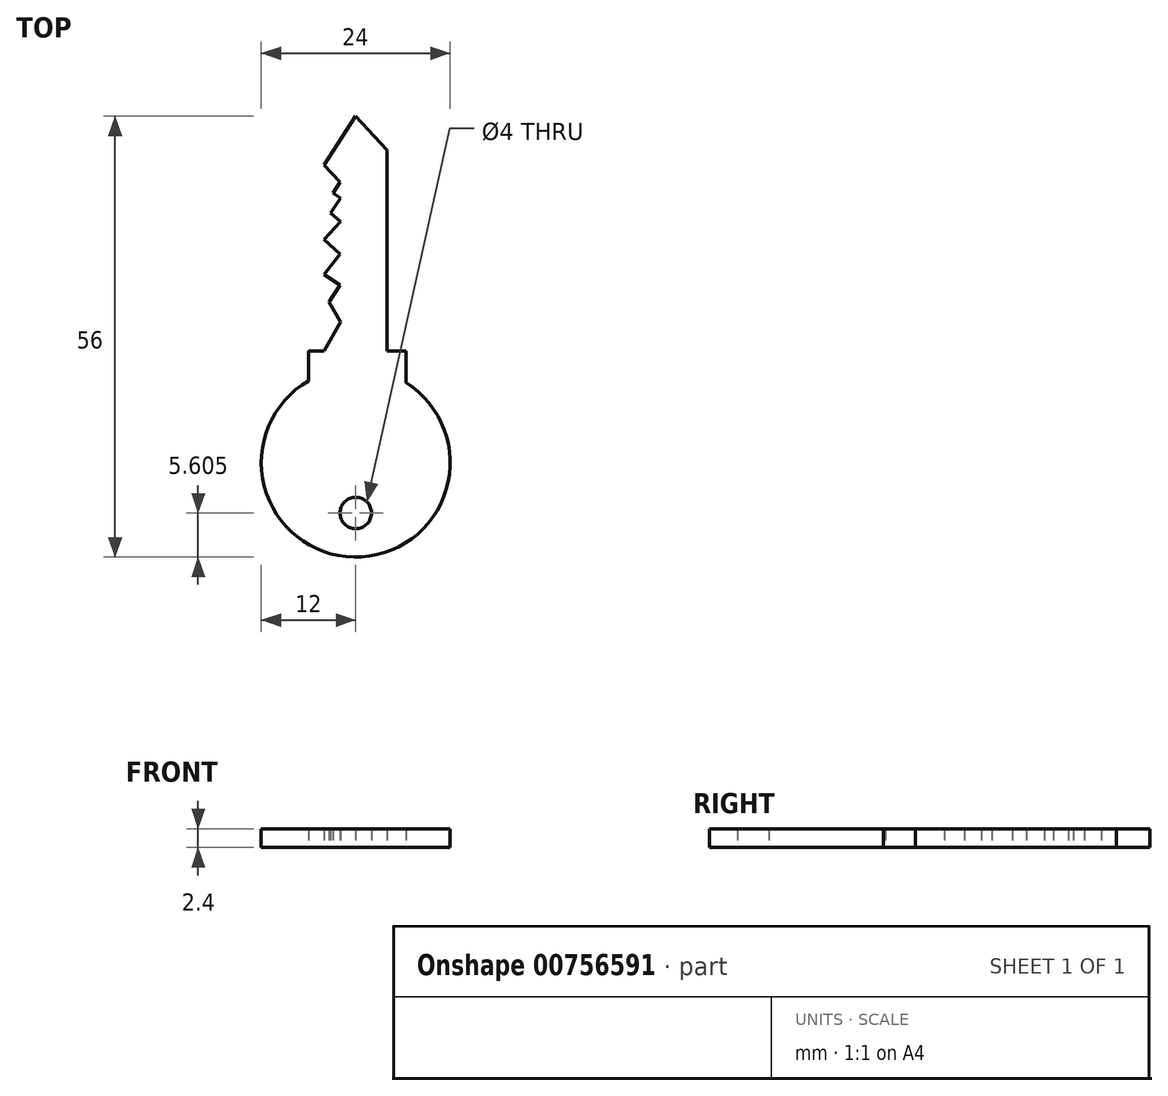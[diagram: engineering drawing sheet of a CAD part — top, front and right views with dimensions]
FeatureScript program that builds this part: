
annotation { "Feature Type Name" : "Feature", "Feature Type Description" : "" }
export const myFeature = defineFeature(function(context is Context, id is Id, definition is map)
    precondition{}
    {
        {
            var Q0;
            Q0=qCreatedBy(makeId("Top.planeOp"),FACE);
            var sketch = newSketch(context, id + "F0", { "sketchPlane" : qUnion([Q0])});
            skCircle(sketch, "E0", {"center": v(-4, -2.46) * mm, "radius": 12 * mm});
            skCircle(sketch, "E1", {"center": v(-4, -8.86) * mm, "radius": 2 * mm});
            skLineSegment(sketch, "E2", {"start": v(-4, -2.46) * mm, "end": v(-4, 41.54) * mm});
            skLineSegment(sketch, "E3", {"start": v(-10, 11.71) * mm, "end": v(-10, 7.94) * mm});
            skLineSegment(sketch, "E4", {"start": v(2.4, 11.71) * mm, "end": v(2.4, 7.7) * mm});
            skLineSegment(sketch, "E5", {"start": v(2.4, 11.71) * mm, "end": v(-10, 11.71) * mm});
            skLineSegment(sketch, "E6", {"start": v(-4, 11.71) * mm, "end": v(0, 11.71) * mm});
            skPoint(sketch, "E6.startSnap0", {"position": v(-3.8, 11.71) * mm});
            skLineSegment(sketch, "E7", {"start": v(0, 11.71) * mm, "end": v(-8, 11.71) * mm});
            skLineSegment(sketch, "E8.bottom", {"start": v(-8, 11.71) * mm, "end": v(0, 11.71) * mm});
            skLineSegment(sketch, "E8.top", {"start": v(-8, 11.71) * mm, "end": v(0, 11.71) * mm});
            skLineSegment(sketch, "E8.left", {"start": v(-8, 11.71) * mm, "end": v(-8, 11.71) * mm});
            skLineSegment(sketch, "E8.right", {"start": v(0, 11.71) * mm, "end": v(0, 11.71) * mm});
            skLineSegment(sketch, "E9", {"start": v(0, 11.71) * mm, "end": v(0, 37.26) * mm});
            skLineSegment(sketch, "E10", {"start": v(-8, 26.63) * mm, "end": v(-8, 25.86) * mm});
            skLineSegment(sketch, "E11", {"start": v(-4, 41.54) * mm, "end": v(-8, 35.36) * mm});
            skLineSegment(sketch, "E12", {"start": v(-8, 35.36) * mm, "end": v(-4, 41.54) * mm});
            skLineSegment(sketch, "E13", {"start": v(-4, 41.54) * mm, "end": v(0, 37.26) * mm});
            skLineSegment(sketch, "E14", {"start": v(-8, 35.36) * mm, "end": v(-6, 33.17) * mm});
            skPoint(sketch, "E14.endSnap0", {"position": v(-6, 38.45) * mm});
            skLineSegment(sketch, "E15", {"start": v(-6, 33.17) * mm, "end": v(-6.9, 31.79) * mm});
            skLineSegment(sketch, "E16", {"start": v(-6.9, 31.79) * mm, "end": v(-5.96, 31.18) * mm});
            skLineSegment(sketch, "E17", {"start": v(-5.96, 31.18) * mm, "end": v(-7.2, 29.26) * mm});
            skLineSegment(sketch, "E18", {"start": v(-7.2, 29.26) * mm, "end": v(-5.96, 28.14) * mm});
            skLineSegment(sketch, "E19", {"start": v(-5.96, 28.14) * mm, "end": v(-8, 25.86) * mm});
            skPoint(sketch, "E19.endSnap0", {"position": v(-8, 26.63) * mm});
            skLineSegment(sketch, "E20", {"start": v(-8, 25.86) * mm, "end": v(-6, 24.07) * mm});
            skLineSegment(sketch, "E21", {"start": v(-6, 24.07) * mm, "end": v(-8, 21.42) * mm});
            skLineSegment(sketch, "E22", {"start": v(-8, 21.42) * mm, "end": v(-6, 20.13) * mm});
            skLineSegment(sketch, "E23", {"start": v(-6, 20.13) * mm, "end": v(-7.41, 17.95) * mm});
            skLineSegment(sketch, "E24", {"start": v(-7.41, 17.95) * mm, "end": v(-5.96, 15.42) * mm});
            skLineSegment(sketch, "E25", {"start": v(-5.96, 15.42) * mm, "end": v(-8, 11.71) * mm});
            skLineSegment(sketch, "E26", {"start": v(-4, 11.71) * mm, "end": v(-4.8, 11.71) * mm});
            skLineSegment(sketch, "E27", {"start": v(-4.8, 11.71) * mm, "end": v(-3.2, 11.71) * mm});
            skLineSegment(sketch, "E28", {"start": v(-3.2, 11.71) * mm, "end": v(-3.2, 40.69) * mm});
            skLineSegment(sketch, "E29", {"start": v(-4.55, 40.69) * mm, "end": v(-4.8, 11.71) * mm});
            skPoint(sketch, "E30.orphan", {"position": v(-8, 41.54) * mm});
            skSolve(sketch);
        }
        {
            var Q0;
            {var subQ3=sQuery(id+"F0.wireOp",EDGE,"E14");Q0=makeQuery(id+"F0.imprint","IMPRINT",FACE,{"disambiguationData":[TD([[makeQuery(id+"F0.imprint","IMPRINT",EDGE,{"derivedFrom":subQ3}),1.0]])]});}
            var Q1;
            {var subQ0=sQuery(id+"F0.wireOp",EDGE,"E9");Q1=makeQuery(id+"F0.imprint","IMPRINT",FACE,{"disambiguationData":[TD([[makeQuery(id+"F0.imprint","IMPRINT",EDGE,{"derivedFrom":subQ0}),1.0]])]});}
            var Q2;
            {var subQ1=sQuery(id+"F0.wireOp",EDGE,"E3");Q2=makeQuery(id+"F0.imprint","IMPRINT",FACE,{"disambiguationData":[TD([[makeQuery(id+"F0.imprint","IMPRINT",EDGE,{"derivedFrom":subQ1}),1.0]])]});}
            var Q3;
            {var subQ0=sQuery(id+"F0.wireOp",EDGE,"E4");Q3=makeQuery(id+"F0.imprint","IMPRINT",FACE,{"disambiguationData":[TD([[makeQuery(id+"F0.imprint","IMPRINT",EDGE,{"derivedFrom":subQ0}),-1.0]])]});}
            var Q4;
            Q4=makeQuery(id+"F0.imprint","IMPRINT",FACE,{"disambiguationData":[TD([[makeQuery(id+"F0.imprint","IMPRINT",EDGE,{"derivedFrom":sQuery(id+"F0.wireOp",EDGE,"E1")}),-1.0]])]});
            var Q5;
            {var subQ5=sQuery(id+"F0.wireOp",EDGE,"E28");Q5=makeQuery(id+"F0.imprint","IMPRINT",FACE,{"disambiguationData":[TD([[makeQuery(id+"F0.imprint","IMPRINT",EDGE,{"derivedFrom":subQ5}),1.0]])]});}
            var Q6;
            {var subQ5=sQuery(id+"F0.wireOp",EDGE,"E29");Q6=makeQuery(id+"F0.imprint","IMPRINT",FACE,{"disambiguationData":[TD([[makeQuery(id+"F0.imprint","IMPRINT",EDGE,{"derivedFrom":subQ5}),1.0]])]});}
            extrude(context, id + "F1", {"entities" : qUnion([Q0, Q1, Q2, Q3, Q4, Q5, Q6]), "depth" : 2.4 * mm, "offsetDistance" : 25 * mm});
        }
    });
